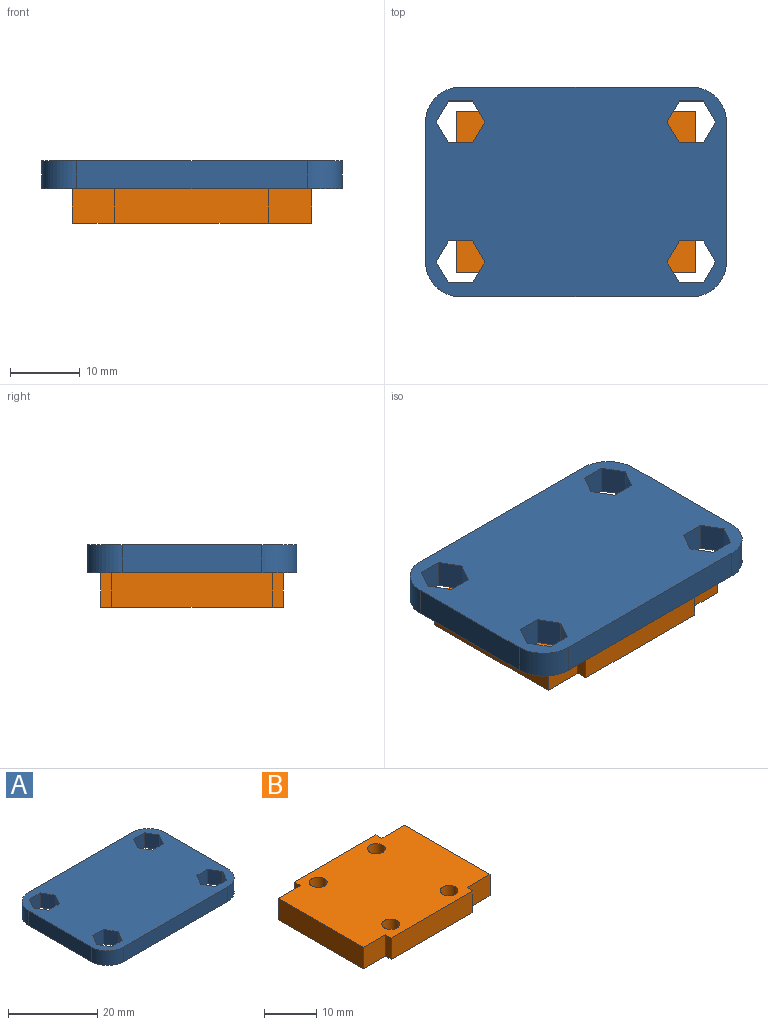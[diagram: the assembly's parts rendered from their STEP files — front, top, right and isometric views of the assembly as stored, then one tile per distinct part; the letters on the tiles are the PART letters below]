
ASSEMBLY  parts=2 mates=1
PART A: 34 faces, bbox 43x30x4 mm
  f0: plane 20x4mm, normal (-1,0,0), area 80mm2, adj f4,f5,f6,f9
  f1: plane 33x4mm, normal (0,-1,0), area 132mm2, adj f4,f5,f6,f7
  f2: plane 20x4mm, normal (1,0,0), area 80mm2, adj f4,f5,f7,f8
  f3: plane 33x4mm, normal (0,1,0), area 132mm2, adj f4,f5,f8,f9
  f4: plane 43x30mm, normal (0,0,-1), area 1143.8mm2, adj f0,f1,f2,f3,f6,f7,f8,f9
  f5: plane 43x30mm, normal (0,0,1), area 1143.8mm2, adj f0,f1,f2,f3,f6,f7,f8,f9
  f6: cylinder r=5mm len=5mm, axis (0,0,-1), area 31.4mm2, adj f0,f1,f4,f5
  f7: cylinder r=5mm len=5mm, axis (0,0,1), area 31.4mm2, adj f1,f2,f4,f5
  f8: cylinder r=5mm len=5mm, axis (0,0,-1), area 31.4mm2, adj f2,f3,f4,f5
  f9: cylinder r=5mm len=5mm, axis (0,0,1), area 31.4mm2, adj f0,f3,f4,f5
  f10: plane 4x3mm, normal (0.87,0.5,0), area 13.9mm2, adj f4,f5,f11,f15
  f11: plane 4x3.46mm, normal (0,1,0), area 13.9mm2, adj f4,f5,f10,f12
  f12: plane 4x3mm, normal (-0.87,0.5,0), area 13.9mm2, adj f4,f5,f11,f13
  f13: plane 4x3mm, normal (-0.87,-0.5,0), area 13.9mm2, adj f4,f5,f12,f14
  f14: plane 4x3.46mm, normal (0,-1,0), area 13.9mm2, adj f4,f5,f13,f15
  f15: plane 4x3mm, normal (0.87,-0.5,0), area 13.9mm2, adj f4,f5,f10,f14
  f16: plane 4x3mm, normal (-0.87,-0.5,0), area 13.9mm2, adj f4,f5,f17,f21
  f17: plane 4x3.46mm, normal (0,-1,0), area 13.9mm2, adj f4,f5,f16,f18
  f18: plane 4x3mm, normal (0.87,-0.5,0), area 13.9mm2, adj f4,f5,f17,f19
  f19: plane 4x3mm, normal (0.87,0.5,0), area 13.9mm2, adj f4,f5,f18,f20
  f20: plane 4x3.46mm, normal (0,1,0), area 13.9mm2, adj f4,f5,f19,f21
  f21: plane 4x3mm, normal (-0.87,0.5,0), area 13.9mm2, adj f4,f5,f16,f20
  f22: plane 4x3mm, normal (-0.87,-0.5,0), area 13.9mm2, adj f4,f5,f23,f27
  f23: plane 4x3.46mm, normal (0,-1,0), area 13.9mm2, adj f4,f5,f22,f24
  f24: plane 4x3mm, normal (0.87,-0.5,0), area 13.9mm2, adj f4,f5,f23,f25
  f25: plane 4x3mm, normal (0.87,0.5,0), area 13.9mm2, adj f4,f5,f24,f26
  f26: plane 4x3.46mm, normal (0,1,0), area 13.9mm2, adj f4,f5,f25,f27
  f27: plane 4x3mm, normal (-0.87,0.5,0), area 13.9mm2, adj f4,f5,f22,f26
  f28: plane 4x3mm, normal (-0.87,-0.5,0), area 13.9mm2, adj f4,f5,f29,f33
  f29: plane 4x3.46mm, normal (0,-1,0), area 13.9mm2, adj f4,f5,f28,f30
  f30: plane 4x3mm, normal (0.87,-0.5,0), area 13.9mm2, adj f4,f5,f29,f31
  f31: plane 4x3mm, normal (0.87,0.5,0), area 13.9mm2, adj f4,f5,f30,f32
  f32: plane 4x3.46mm, normal (0,1,0), area 13.9mm2, adj f4,f5,f31,f33
  f33: plane 4x3mm, normal (-0.87,0.5,0), area 13.9mm2, adj f4,f5,f28,f32
PART B: 18 faces, bbox 34.2x26.2x5 mm
  f0: plane 5x1.6mm, normal (1,0,0), area 8mm2, adj f1,f11,f12,f13
  f1: plane 6.2x5mm, normal (0,-1,0), area 31mm2, adj f0,f2,f12,f13
  f2: plane 22.95x5mm, normal (1,0,0), area 114.8mm2, adj f1,f3,f12,f13
  f3: plane 6.2x5mm, normal (0,1,0), area 31mm2, adj f2,f4,f12,f13
  f4: plane 5x1.6mm, normal (1,0,0), area 8mm2, adj f3,f5,f12,f13
  f5: plane 22x5mm, normal (0,1,0), area 110mm2, adj f4,f6,f12,f13
  f6: plane 5x1.6mm, normal (-1,0,0), area 8mm2, adj f5,f7,f12,f13
  f7: plane 6x5mm, normal (0,1,0), area 30mm2, adj f6,f8,f12,f13
  f8: plane 22.95x5mm, normal (-1,0,0), area 114.8mm2, adj f7,f9,f12,f13
  f9: plane 6x5mm, normal (0,-1,0), area 30mm2, adj f8,f10,f12,f13
  f10: plane 5x1.6mm, normal (-1,0,0), area 8mm2, adj f9,f11,f12,f13
  f11: plane 22x5mm, normal (0,-1,0), area 110mm2, adj f0,f10,f12,f13
  f12: plane 34.2x26.15mm, normal (0,0,1), area 819mm2, adj f0,f1,f2,f3,f4,f5,f6,f7
  f13: plane 34.2x26.15mm, normal (0,0,-1), area 819mm2, adj f0,f1,f2,f3,f4,f5,f6,f7
  f14: cylinder r=1.7mm len=5mm, axis (0,0,1), area 53.4mm2, adj f12,f13
  f15: cylinder r=1.7mm len=5mm, axis (0,0,1), area 53.4mm2, adj f12,f13
  f16: cylinder r=1.7mm len=5mm, axis (0,0,1), area 53.4mm2, adj f12,f13
  f17: cylinder r=1.7mm len=5mm, axis (0,0,1), area 53.4mm2, adj f12,f13
PLACE A t=(4.62,-5.46,-11.79)mm
PLACE B t=(9.02,-1.93,-20.79)mm
MATE fastened A.f4 <-> B.f12  axis (0,0,-1) through (26.12,9.54,-15.79)mm
